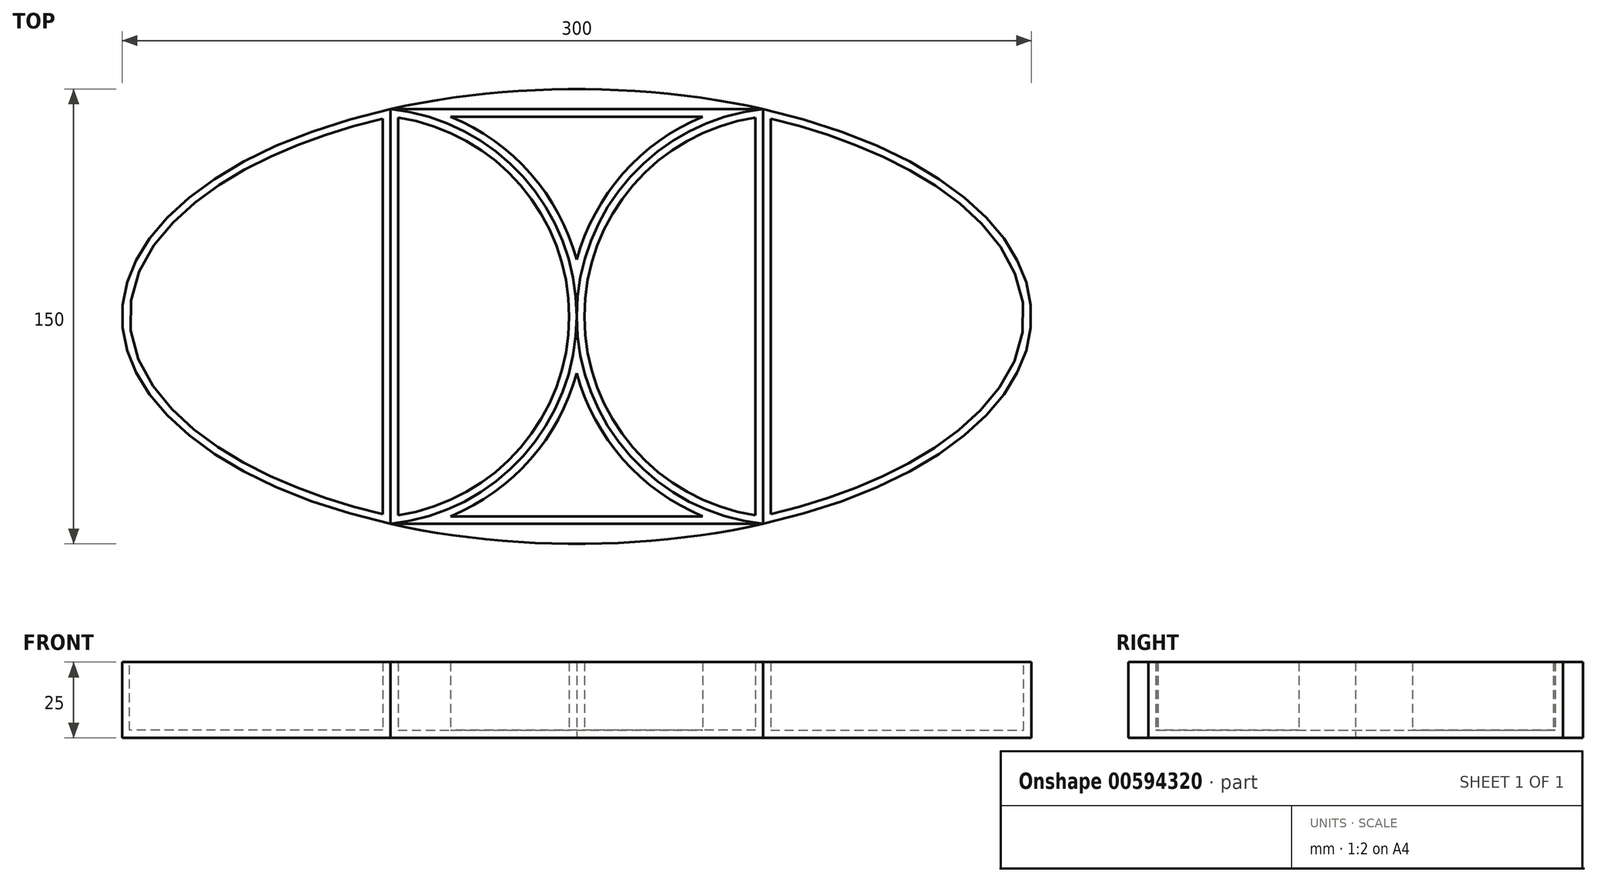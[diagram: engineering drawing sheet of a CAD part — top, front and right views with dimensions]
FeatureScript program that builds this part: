
annotation { "Feature Type Name" : "Feature", "Feature Type Description" : "" }
export const myFeature = defineFeature(function(context is Context, id is Id, definition is map)
    precondition{}
    {
        {
            var Q0;
            Q0=qCreatedBy(makeId("Top.planeOp"),FACE);
            var sketch = newSketch(context, id + "F0", { "sketchPlane" : qUnion([Q0])});
            skEllipse(sketch, "E0", {"center": v(0, 0) * mm, "majorRadius": 150 * mm, "minorRadius": 75 * mm, "majorAxis": v(-1, 0)});
            skPoint(sketch, "E1.endSnap0", {"position": v(0, 75) * mm});
            skLineSegment(sketch, "E2.0", {"start": v(-61.47, -68.41) * mm, "end": v(-61.47, 68.41) * mm});
            skLineSegment(sketch, "E3.MirrorCS", {"start": v(61.47, -68.41) * mm, "end": v(61.47, 68.41) * mm});
            skPoint(sketch, "E4.orphan", {"position": v(61.47, 0) * mm});
            skPoint(sketch, "E5.orphan", {"position": v(-61.47, 0) * mm});
            skPoint(sketch, "E6.orphan", {"position": v(-61.47, 57.56) * mm});
            skPoint(sketch, "E7.orphan", {"position": v(61.47, 57.56) * mm});
            skArc(sketch, "E8", {"start": v(61.47, 68.41) * mm, "mid": v(0, 0) * mm, "end": v(61.47, -68.41) * mm});
            skArc(sketch, "E9.trimOffspring", {"start": v(-61.47, -68.41) * mm, "mid": v(0, 0) * mm, "end": v(-61.47, 68.41) * mm});
            skLineSegment(sketch, "E10", {"start": v(-61.47, 68.41) * mm, "end": v(61.47, 68.41) * mm});
            skLineSegment(sketch, "E11", {"start": v(-61.47, -68.41) * mm, "end": v(61.47, -68.41) * mm});
            skSolve(sketch);
        }
        {
            var Q0;
            {var subQ1=sQuery(id+"F0.wireOp",EDGE,"E2.0");Q0=makeQuery(id+"F0.imprint","IMPRINT",FACE,{"disambiguationData":[TD([[makeQuery(id+"F0.imprint","IMPRINT",EDGE,{"derivedFrom":subQ1}),1.0]])]});}
            var Q1;
            {var subQ1=sQuery(id+"F0.wireOp",EDGE,"E3.MirrorCS");Q1=makeQuery(id+"F0.imprint","IMPRINT",FACE,{"disambiguationData":[TD([[makeQuery(id+"F0.imprint","IMPRINT",EDGE,{"derivedFrom":subQ1}),-1.0]])]});}
            extrude(context, id + "F1", {"entities" : qUnion([Q0, Q1]), "depth" : 25 * mm, "offsetDistance" : 25 * mm});
        }
        {
            var Q0;
            Q0=makeQuery(id+"F1.opExtrude","CAP_FACE",FACE,{"disambiguationData":[OSD([sQuery(id+"F0.wireOp",EDGE,"E0"),sQuery(id+"F0.wireOp",EDGE,"E2.0")])],"isStart":false});
            var Q1;
            Q1=makeQuery(id+"F1.opExtrude","CAP_FACE",FACE,{"disambiguationData":[OSD([sQuery(id+"F0.wireOp",EDGE,"E0"),sQuery(id+"F0.wireOp",EDGE,"E3.MirrorCS")])],"isStart":false});
            shell(context, id + "F2", {"entities" : qUnion([Q0, Q1]), "thickness" : 2.5 * mm});
        }
        {
            var Q0;
            {var subQ0=sQuery(id+"F0.wireOp",EDGE,"E2.0");Q0=makeQuery(id+"F0.imprint","IMPRINT",FACE,{"disambiguationData":[TD([[makeQuery(id+"F0.imprint","IMPRINT",EDGE,{"derivedFrom":subQ0}),-1.0]])]});}
            var Q1;
            {var subQ0=sQuery(id+"F0.wireOp",EDGE,"E3.MirrorCS");Q1=makeQuery(id+"F0.imprint","IMPRINT",FACE,{"disambiguationData":[TD([[makeQuery(id+"F0.imprint","IMPRINT",EDGE,{"derivedFrom":subQ0}),1.0]])]});}
            extrude(context, id + "F3", {"entities" : qUnion([Q0, Q1]), "depth" : 25 * mm, "offsetDistance" : 25 * mm});
        }
        {
            var Q0;
            Q0=makeQuery(id+"F3.opExtrude","CAP_FACE",FACE,{"disambiguationData":[OSD([sQuery(id+"F0.wireOp",EDGE,"E2.0"),sQuery(id+"F0.wireOp",EDGE,"E9.trimOffspring")])],"isStart":false});
            var Q1;
            Q1=makeQuery(id+"F3.opExtrude","CAP_FACE",FACE,{"disambiguationData":[OSD([sQuery(id+"F0.wireOp",EDGE,"E3.MirrorCS"),sQuery(id+"F0.wireOp",EDGE,"E8")])],"isStart":false});
            shell(context, id + "F4", {"entities" : qUnion([Q0, Q1]), "thickness" : 2.5 * mm});
        }
        {
            var Q0;
            {var subQ0=sQuery(id+"F0.wireOp",EDGE,"E10");Q0=makeQuery(id+"F0.imprint","IMPRINT",FACE,{"disambiguationData":[TD([[makeQuery(id+"F0.imprint","IMPRINT",EDGE,{"derivedFrom":subQ0}),-1.0]])]});}
            var Q1;
            {var subQ0=sQuery(id+"F0.wireOp",EDGE,"E11");Q1=makeQuery(id+"F0.imprint","IMPRINT",FACE,{"disambiguationData":[TD([[makeQuery(id+"F0.imprint","IMPRINT",EDGE,{"derivedFrom":subQ0}),1.0]])]});}
            extrude(context, id + "F5", {"entities" : qUnion([Q0, Q1]), "depth" : 25 * mm, "offsetDistance" : 25 * mm});
        }
        {
            var Q0;
            Q0=makeQuery(id+"F5.opExtrude","CAP_FACE",FACE,{"disambiguationData":[OSD([sQuery(id+"F0.wireOp",EDGE,"E8"),sQuery(id+"F0.wireOp",EDGE,"E9.trimOffspring"),sQuery(id+"F0.wireOp",EDGE,"E10")])],"isStart":false});
            shell(context, id + "F6", {"entities" : qUnion([Q0]), "thickness" : 2.5 * mm});
        }
        {
            var Q0;
            Q0=makeQuery(id+"F5.opExtrude","CAP_FACE",FACE,{"disambiguationData":[OSD([sQuery(id+"F0.wireOp",EDGE,"E8"),sQuery(id+"F0.wireOp",EDGE,"E9.trimOffspring"),sQuery(id+"F0.wireOp",EDGE,"E11")])],"isStart":false});
            shell(context, id + "F7", {"entities" : qUnion([Q0]), "thickness" : 2.5 * mm});
        }
        {
            var Q0;
            {var subQ0=sQuery(id+"F0.wireOp",EDGE,"E10");Q0=makeQuery(id+"F0.imprint","IMPRINT",FACE,{"disambiguationData":[TD([[makeQuery(id+"F0.imprint","IMPRINT",EDGE,{"derivedFrom":subQ0}),1.0]])]});}
            var Q1;
            {var subQ0=sQuery(id+"F0.wireOp",EDGE,"E11");Q1=makeQuery(id+"F0.imprint","IMPRINT",FACE,{"disambiguationData":[TD([[makeQuery(id+"F0.imprint","IMPRINT",EDGE,{"derivedFrom":subQ0}),-1.0]])]});}
            extrude(context, id + "F8", {"entities" : qUnion([Q0, Q1]), "depth" : 25 * mm, "offsetDistance" : 25 * mm});
        }
    });
